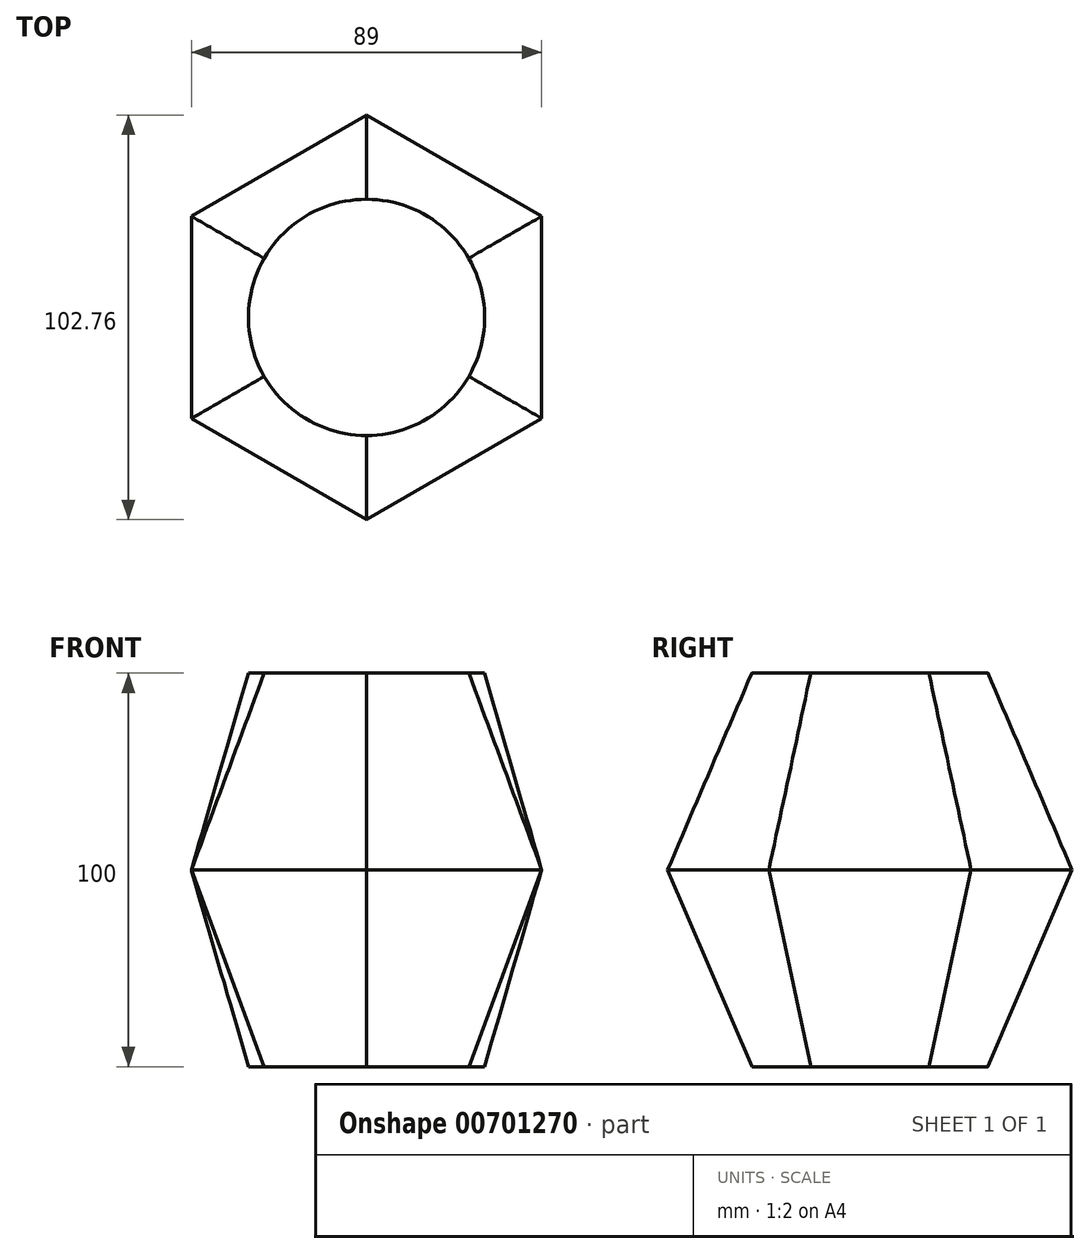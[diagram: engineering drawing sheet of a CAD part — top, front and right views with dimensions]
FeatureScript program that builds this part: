
annotation { "Feature Type Name" : "Feature", "Feature Type Description" : "" }
export const myFeature = defineFeature(function(context is Context, id is Id, definition is map)
    precondition{}
    {
        {
            var Q0;
            Q0=qCreatedBy(makeId("Top.planeOp"),FACE);
            var sketch = newSketch(context, id + "F0", { "sketchPlane" : qUnion([Q0])});
            skCircle(sketch, "E0", {"center": v(0, 0) * mm, "radius": 30 * mm});
            skSolve(sketch);
        }
        {
            var Q0;
            Q0=qCreatedBy(makeId("Top.planeOp"),FACE);
            cPlane(context, id + "F1", {"entities" : qUnion([Q0]), "cplaneType" : CPlaneType.OFFSET, "offset" : 50 * mm, "width" : 150 * mm, "height" : 150 * mm});
        }
        {
            var Q0;
            Q0=qCreatedBy(id+"F1.planeOp",FACE);
            var sketch = newSketch(context, id + "F2", { "sketchPlane" : qUnion([Q0])});
            skCircle(sketch, "E1.cCircle", {"center": v(0, 0) * mm, "radius": 44.5 * mm, "construction": true});
            skLineSegment(sketch, "E1.0", {"start": v(44.5, -25.68) * mm, "end": v(0.01, -51.38) * mm});
            skLineSegment(sketch, "E1.1", {"start": v(0.01, -51.38) * mm, "end": v(-44.49, -25.7) * mm});
            skLineSegment(sketch, "E1.2", {"start": v(-44.49, -25.7) * mm, "end": v(-44.5, 25.68) * mm});
            skLineSegment(sketch, "E1.3", {"start": v(-44.5, 25.68) * mm, "end": v(-0.01, 51.38) * mm});
            skLineSegment(sketch, "E1.4", {"start": v(-0.01, 51.38) * mm, "end": v(44.49, 25.7) * mm});
            skLineSegment(sketch, "E1.5", {"start": v(44.49, 25.7) * mm, "end": v(44.5, -25.68) * mm});
            skPoint(sketch, "E1.0.midPoint", {"position": v(22.26, -38.53) * mm});
            skSolve(sketch);
        }
        {
            var Q0;
            Q0 = qSketchRegion(id + "F2", true);
            var Q1;
            Q1 = qSketchRegion(id + "F0", true);
            loft(context, id + "F3", {"sheetProfilesArray" : [{ "sheetProfileEntities" : qUnion([Q0]) }, { "sheetProfileEntities" : qUnion([Q1]) }]});
        }
        {
            var Q0;
            Q0=makeQuery(id+"F3.opLoft","SWEPT_BODY",BODY,{"disambiguationData":[OSD([makeQuery(id+"F0.imprint","IMPRINT",FACE,{"disambiguationData":[TD([[makeQuery(id+"F0.imprint","IMPRINT",EDGE,{"derivedFrom":sQuery(id+"F0.wireOp",EDGE,"E0")}),1.0]])]}),makeQuery(id+"F2.imprint","IMPRINT",FACE,{"disambiguationData":[TD([[makeQuery(id+"F2.imprint","IMPRINT",EDGE,{"derivedFrom":sQuery(id+"F2.wireOp",EDGE,"E1.0")}),-1.0]])]})])]});
            var Q1;
            Q1=qCreatedBy(id+"F1.planeOp",FACE);
            mirror(context, id + "F4", {"operationType" : NewBodyOperationType.ADD, "entities" : qUnion([Q0]), "mirrorPlane" : qUnion([Q1])});
        }
    });
